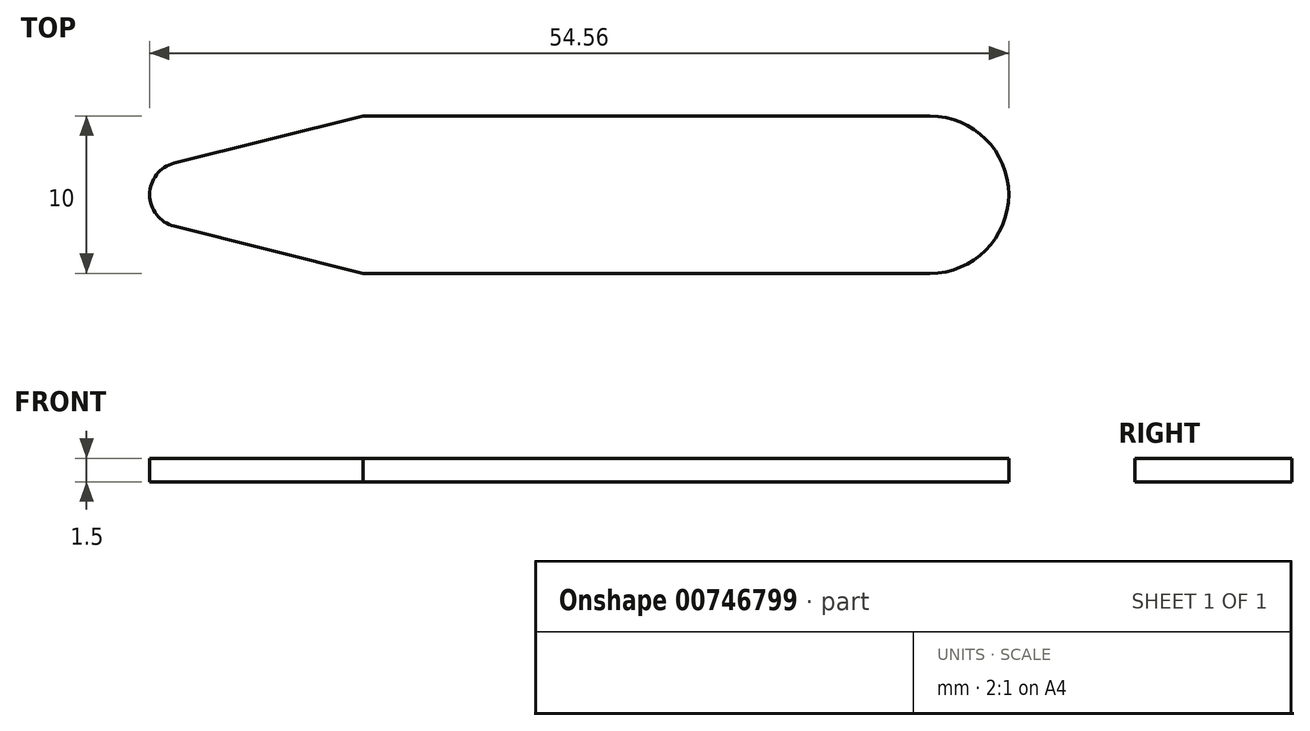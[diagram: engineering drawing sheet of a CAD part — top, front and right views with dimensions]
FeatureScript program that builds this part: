
annotation { "Feature Type Name" : "Feature", "Feature Type Description" : "" }
export const myFeature = defineFeature(function(context is Context, id is Id, definition is map)
    precondition{}
    {
        {
            var Q0;
            Q0=qCreatedBy(makeId("Top.planeOp"),FACE);
            var sketch = newSketch(context, id + "F0", { "sketchPlane" : qUnion([Q0])});
            skLineSegment(sketch, "E0.bottom", {"start": v(18, -5) * mm, "end": v(-18, -5) * mm});
            skLineSegment(sketch, "E0.top", {"start": v(18, 5) * mm, "end": v(-18, 5) * mm});
            skLineSegment(sketch, "E0.left", {"start": v(18, -5) * mm, "end": v(18, 5) * mm});
            skLineSegment(sketch, "E0.right", {"start": v(-18, -5) * mm, "end": v(-18, 5) * mm});
            skPoint(sketch, "E0.middle", {"position": v(0, 0) * mm});
            skArc(sketch, "E1", {"start": v(18, -5) * mm, "mid": v(23, 0) * mm, "end": v(18, 5) * mm});
            skPoint(sketch, "E2.startSnap0", {"position": v(-18, 0) * mm});
            skLineSegment(sketch, "E3", {"start": v(-18, 5) * mm, "end": v(-30, 2) * mm});
            skLineSegment(sketch, "E4", {"start": v(-30, -2) * mm, "end": v(-18, -5) * mm});
            skArc(sketch, "E5", {"start": v(-30, 2) * mm, "mid": v(-31.56, 0) * mm, "end": v(-30, -2) * mm});
            skSolve(sketch);
        }
        {
            var Q0;
            Q0 = qSketchRegion(id + "F0", true);
            extrude(context, id + "F1", {"entities" : qUnion([Q0]), "depth" : 1.5 * mm, "offsetDistance" : 25 * mm});
        }
    });
